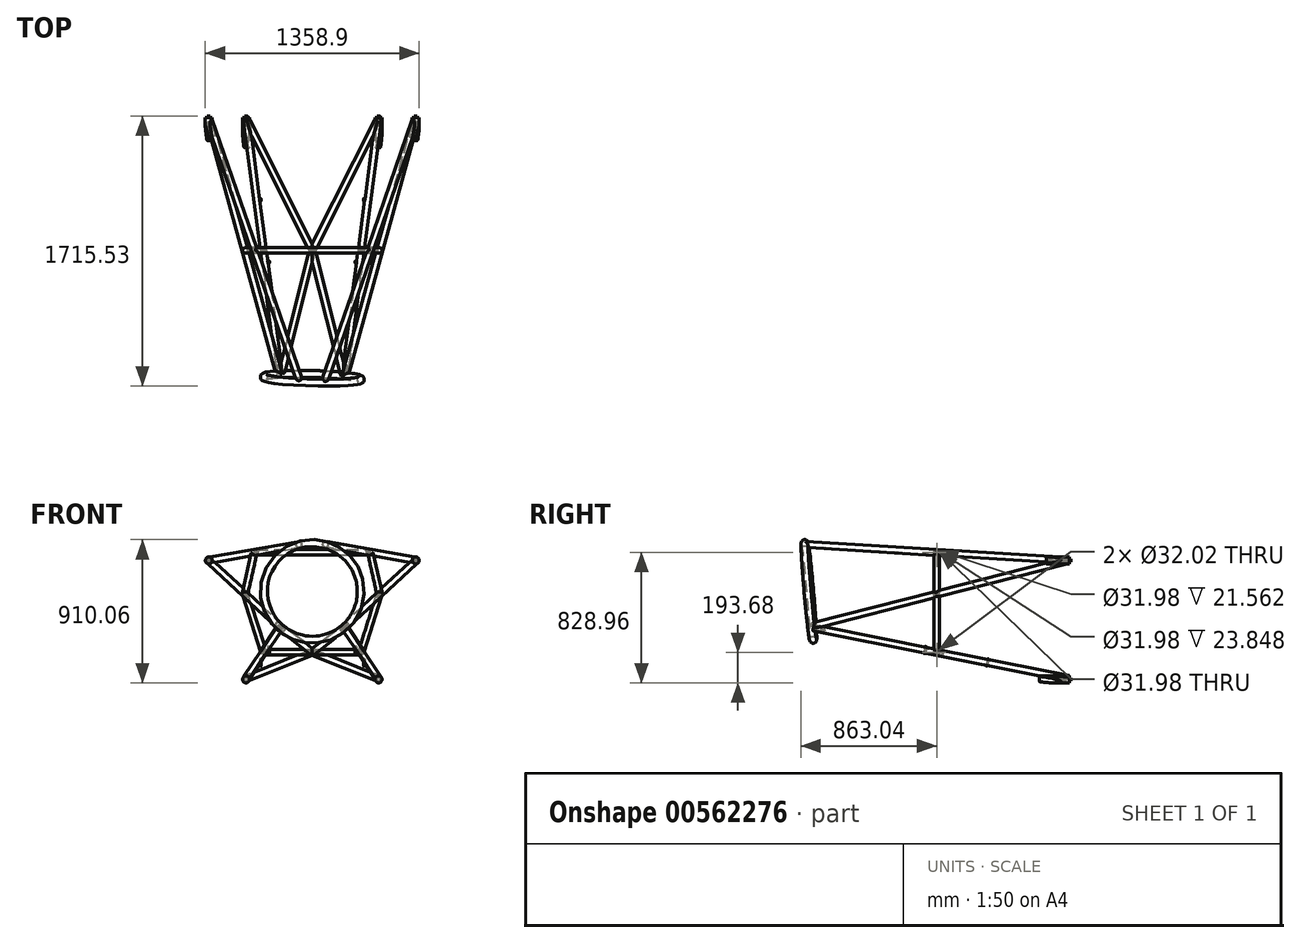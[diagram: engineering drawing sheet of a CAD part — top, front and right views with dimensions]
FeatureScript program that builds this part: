
annotation { "Feature Type Name" : "Feature", "Feature Type Description" : "" }
export const myFeature = defineFeature(function(context is Context, id is Id, definition is map)
    precondition{}
    {
        {
            var Q0;
            Q0=qCreatedBy(makeId("Front.planeOp"),FACE);
            var sketch = newSketch(context, id + "F0", { "sketchPlane" : qUnion([Q0])});
            skCircle(sketch, "E0", {"center": v(0, 0) * mm, "radius": 285.75 * mm});
            skPoint(sketch, "E1", {"position": v(0, 285.75) * mm});
            skPoint(sketch, "E2", {"position": v(0, -285.75) * mm});
            skPoint(sketch, "E3", {"position": v(285.75, 0) * mm});
            skPoint(sketch, "E4", {"position": v(-285.75, 0) * mm});
            skLineSegment(sketch, "E5", {"start": v(0, 285.75) * mm, "end": v(0, -285.75) * mm, "construction": true});
            skLineSegment(sketch, "E6", {"start": v(285.75, 0) * mm, "end": v(-285.75, 0) * mm, "construction": true});
            skSolve(sketch);
        }
        {
            var Q0;
            Q0=qCreatedBy(makeId("Right.planeOp"),FACE);
            var sketch = newSketch(context, id + "F1", { "sketchPlane" : qUnion([Q0])});
            skCircle(sketch, "E7", {"center": v(0, 307.98) * mm, "radius": 22.23 * mm});
            skSolve(sketch);
        }
        {
            var Q0;
            Q0=qSketchRegion(id+"F1",true);
            var Q1;
            Q1=sQuery(id+"F0.wireOp",EDGE,"E0");
            revolve(context, id + "F2", {"surfaceOperationType" : NewSurfaceOperationType.NEW, "entities" : qUnion([Q0]), "axis" : qUnion([Q1]), "revolveType" : RevolveType.FULL});
        }
        {
            var Q0;
            Q0=qCreatedBy(makeId("Front.planeOp"),FACE);
            var sketch = newSketch(context, id + "F3", { "sketchPlane" : qUnion([Q0])});
            skCircle(sketch, "E8", {"center": v(0, 0) * mm, "radius": 307.98 * mm, "construction": true});
            skSolve(sketch);
        }
        {
            var Q0;
            Q0=qCreatedBy(makeId("Front.planeOp"),FACE);
            cPlane(context, id + "F4", {"entities" : qUnion([Q0]), "cplaneType" : CPlaneType.OFFSET, "offset" : 1654.17 * mm, "oppositeDirection" : true, "width" : 152.4 * mm, "height" : 152.4 * mm});
        }
        {
            var Q0;
            Q0=qCreatedBy(makeId("Right.planeOp"),FACE);
            var sketch = newSketch(context, id + "F5", { "sketchPlane" : qUnion([Q0])});
            skLineSegment(sketch, "E9", {"start": v(1501.77, 196.85) * mm, "end": v(1665.29, 196.85) * mm});
            skLineSegment(sketch, "E10", {"start": v(1665.29, 196.85) * mm, "end": v(1665.29, 196.85) * mm});
            skLineSegment(sketch, "E11", {"start": v(1665.29, 187.33) * mm, "end": v(1654.18, 187.33) * mm});
            skLineSegment(sketch, "E12", {"start": v(1654.18, 187.33) * mm, "end": v(1654.18, 174.63) * mm});
            skLineSegment(sketch, "E13", {"start": v(1654.18, 174.63) * mm, "end": v(1501.78, 174.63) * mm});
            skLineSegment(sketch, "E14", {"start": v(1501.78, 174.63) * mm, "end": v(1501.78, 178.4) * mm});
            skLineSegment(sketch, "E15", {"start": v(1501.77, 178.4) * mm, "end": v(1638.3, 178.4) * mm});
            skLineSegment(sketch, "E16", {"start": v(1641.48, 181.57) * mm, "end": v(1641.48, 191.3) * mm});
            skLineSegment(sketch, "E17", {"start": v(1641.48, 196.85) * mm, "end": v(1665.29, 196.85) * mm, "construction": true});
            skLineSegment(sketch, "E18", {"start": v(1665.29, 196.85) * mm, "end": v(1665.29, 191.3) * mm});
            skPoint(sketch, "E19.visualSharp", {"position": v(1641.48, 178.4) * mm});
            skArc(sketch, "E19.filletArc", {"start": v(1638.3, 178.4) * mm, "mid": v(1640.55, 179.32) * mm, "end": v(1641.48, 181.57) * mm});
            skLineSegment(sketch, "E20", {"start": v(1641.48, 191.3) * mm, "end": v(1665.29, 191.3) * mm});
            skLineSegment(sketch, "E21", {"start": v(1641.48, 191.3) * mm, "end": v(1641.48, 196.85) * mm, "construction": true});
            skLineSegment(sketch, "E22", {"start": v(1665.29, 191.3) * mm, "end": v(1665.29, 187.33) * mm});
            skLineSegment(sketch, "E23", {"start": v(1501.77, 196.85) * mm, "end": v(1501.77, 178.4) * mm});
            skSolve(sketch);
        }
        {
            var Q0;
            Q0=qSketchRegion(id+"F5",true);
            var Q1;
            Q1=sQuery(id+"F5.wireOp",EDGE,"E9");
            revolve(context, id + "F6", {"surfaceOperationType" : NewSurfaceOperationType.NEW, "entities" : qUnion([Q0]), "axis" : qUnion([Q1]), "revolveType" : RevolveType.FULL});
        }
        {
            var Q0;
            Q0=qCreatedBy(makeId("Right.planeOp"),FACE);
            var sketch = newSketch(context, id + "F7", { "sketchPlane" : qUnion([Q0])});
            skLineSegment(sketch, "E24", {"start": v(1501.78, 219.08) * mm, "end": v(1603.38, 219.08) * mm});
            skLineSegment(sketch, "E25", {"start": v(1603.38, 219.08) * mm, "end": v(1513.37, 203.2) * mm});
            skLineSegment(sketch, "E26", {"start": v(1508.13, 196.95) * mm, "end": v(1508.13, 174.63) * mm});
            skLineSegment(sketch, "E27", {"start": v(1508.13, 174.63) * mm, "end": v(1501.78, 174.63) * mm});
            skLineSegment(sketch, "E28", {"start": v(1501.78, 174.63) * mm, "end": v(1501.78, 219.08) * mm});
            skPoint(sketch, "E29.visualSharp", {"position": v(1508.13, 202.28) * mm});
            skArc(sketch, "E29.filletArc", {"start": v(1513.37, 203.2) * mm, "mid": v(1509.61, 201.03) * mm, "end": v(1508.13, 196.95) * mm});
            skLineSegment(sketch, "E30", {"start": v(1501.78, 196.85) * mm, "end": v(1665.29, 196.85) * mm, "construction": true});
            skSolve(sketch);
        }
        {
            var Q0;
            Q0=qSketchRegion(id+"F7",true);
            extrude(context, id + "F8", {"entities" : qUnion([Q0]), "operationType" : NewBodyOperationType.REMOVE, "endBound" : BoundingType.THROUGH_ALL, "depth" : 25.4 * mm, "offsetDistance" : 25.4 * mm, "hasSecondDirection" : true, "secondDirectionBound" : BoundingType.THROUGH_ALL, "secondDirectionOppositeDirection" : true, "secondDirectionDepth" : 25.4 * mm});
        }
        {
            var Q0;
            Q0=makeQuery(id+"F6.opRevolve","SWEPT_BODY",BODY,{"disambiguationData":[OSD([sQuery(id+"F5.wireOp",EDGE,"E11"),sQuery(id+"F5.wireOp",EDGE,"E12"),sQuery(id+"F5.wireOp",EDGE,"E13"),sQuery(id+"F5.wireOp",EDGE,"E14"),sQuery(id+"F5.wireOp",EDGE,"E15"),sQuery(id+"F5.wireOp",EDGE,"E16"),sQuery(id+"F5.wireOp",EDGE,"E19.filletArc"),sQuery(id+"F5.wireOp",EDGE,"E20"),sQuery(id+"F5.wireOp",EDGE,"E22")])]});
            var Q1;
            Q1=qCreatedBy(makeId("Right.planeOp"),FACE);
            transform(context, id + "F9", {"entities" : qUnion([Q0]), "transformType" : TransformType.TRANSLATION_DISTANCE, "transformDirection" : qUnion([Q1]), "distance" : 657.22 * mm, "makeCopy" : true});
        }
        {
            var Q0;
            Q0=makeQuery(id+"F6.opRevolve","SWEPT_BODY",BODY,{"disambiguationData":[OSD([sQuery(id+"F5.wireOp",EDGE,"E11"),sQuery(id+"F5.wireOp",EDGE,"E12"),sQuery(id+"F5.wireOp",EDGE,"E13"),sQuery(id+"F5.wireOp",EDGE,"E14"),sQuery(id+"F5.wireOp",EDGE,"E15"),sQuery(id+"F5.wireOp",EDGE,"E16"),sQuery(id+"F5.wireOp",EDGE,"E19.filletArc"),sQuery(id+"F5.wireOp",EDGE,"E20"),sQuery(id+"F5.wireOp",EDGE,"E22")])]});
            var Q1;
            Q1=qCreatedBy(makeId("Right.planeOp"),FACE);
            transform(context, id + "F10", {"entities" : qUnion([Q0]), "transformType" : TransformType.TRANSLATION_DISTANCE, "transformDirection" : qUnion([Q1]), "distance" : 657.22 * mm, "oppositeDirection" : true, "makeCopy" : false});
        }
        {
            var Q0;
            Q0=qCreatedBy(makeId("Right.planeOp"),FACE);
            var sketch = newSketch(context, id + "F11", { "sketchPlane" : qUnion([Q0])});
            skLineSegment(sketch, "E31", {"start": v(1457.33, -558.8) * mm, "end": v(1665.29, -558.8) * mm});
            skLineSegment(sketch, "E32", {"start": v(1665.29, -558.8) * mm, "end": v(1665.29, -558.8) * mm});
            skLineSegment(sketch, "E33", {"start": v(1665.29, -568.32) * mm, "end": v(1654.18, -568.32) * mm});
            skLineSegment(sketch, "E34", {"start": v(1654.18, -568.32) * mm, "end": v(1654.18, -581.02) * mm});
            skLineSegment(sketch, "E35", {"start": v(1654.18, -581.02) * mm, "end": v(1457.33, -581.02) * mm});
            skLineSegment(sketch, "E36", {"start": v(1457.33, -581.02) * mm, "end": v(1457.33, -577.26) * mm});
            skLineSegment(sketch, "E37", {"start": v(1457.33, -577.26) * mm, "end": v(1638.3, -577.26) * mm});
            skLineSegment(sketch, "E38", {"start": v(1641.48, -574.08) * mm, "end": v(1641.48, -564.36) * mm});
            skLineSegment(sketch, "E39", {"start": v(1641.48, -558.8) * mm, "end": v(1665.29, -558.8) * mm, "construction": true});
            skLineSegment(sketch, "E40", {"start": v(1665.29, -558.8) * mm, "end": v(1665.29, -564.36) * mm});
            skPoint(sketch, "E41.visualSharp", {"position": v(1641.48, -577.26) * mm});
            skArc(sketch, "E41.filletArc", {"start": v(1638.3, -577.26) * mm, "mid": v(1640.55, -576.33) * mm, "end": v(1641.48, -574.08) * mm});
            skLineSegment(sketch, "E42", {"start": v(1641.48, -564.36) * mm, "end": v(1665.29, -564.36) * mm});
            skLineSegment(sketch, "E43", {"start": v(1641.48, -564.36) * mm, "end": v(1641.48, -558.8) * mm, "construction": true});
            skLineSegment(sketch, "E44", {"start": v(1665.29, -564.36) * mm, "end": v(1665.29, -564.36) * mm});
            skLineSegment(sketch, "E45", {"start": v(1665.29, -564.36) * mm, "end": v(1665.29, -568.32) * mm});
            skLineSegment(sketch, "E46", {"start": v(1457.33, -577.26) * mm, "end": v(1457.33, -558.8) * mm});
            skSolve(sketch);
        }
        {
            var Q0;
            Q0=qSketchRegion(id+"F11",true);
            var Q1;
            Q1=sQuery(id+"F11.wireOp",EDGE,"E31");
            revolve(context, id + "F12", {"surfaceOperationType" : NewSurfaceOperationType.NEW, "entities" : qUnion([Q0]), "axis" : qUnion([Q1]), "revolveType" : RevolveType.FULL});
        }
        {
            var Q0;
            Q0=qCreatedBy(makeId("Right.planeOp"),FACE);
            var sketch = newSketch(context, id + "F13", { "sketchPlane" : qUnion([Q0])});
            skLineSegment(sketch, "E47", {"start": v(1457.33, -536.57) * mm, "end": v(1603.38, -536.57) * mm});
            skLineSegment(sketch, "E48", {"start": v(1603.38, -536.57) * mm, "end": v(1468.92, -560.28) * mm});
            skLineSegment(sketch, "E49", {"start": v(1463.68, -566.54) * mm, "end": v(1463.68, -581.02) * mm});
            skLineSegment(sketch, "E50", {"start": v(1463.68, -581.02) * mm, "end": v(1457.33, -581.02) * mm});
            skLineSegment(sketch, "E51", {"start": v(1457.33, -581.02) * mm, "end": v(1457.33, -536.57) * mm});
            skPoint(sketch, "E52.visualSharp", {"position": v(1463.68, -561.2) * mm});
            skArc(sketch, "E52.filletArc", {"start": v(1468.92, -560.28) * mm, "mid": v(1465.16, -562.45) * mm, "end": v(1463.68, -566.54) * mm});
            skLineSegment(sketch, "E53", {"start": v(1457.33, -558.8) * mm, "end": v(1665.29, -558.8) * mm, "construction": true});
            skSolve(sketch);
        }
        {
            var Q0;
            Q0=qSketchRegion(id+"F13",true);
            extrude(context, id + "F14", {"entities" : qUnion([Q0]), "operationType" : NewBodyOperationType.REMOVE, "endBound" : BoundingType.THROUGH_ALL, "depth" : 25.4 * mm, "offsetDistance" : 25.4 * mm, "hasSecondDirection" : true, "secondDirectionBound" : BoundingType.THROUGH_ALL, "secondDirectionOppositeDirection" : true, "secondDirectionDepth" : 25.4 * mm});
        }
        {
            var Q0;
            Q0=makeQuery(id+"F12.opRevolve","SWEPT_BODY",BODY,{"disambiguationData":[OSD([sQuery(id+"F11.wireOp",EDGE,"E33"),sQuery(id+"F11.wireOp",EDGE,"E34"),sQuery(id+"F11.wireOp",EDGE,"E35"),sQuery(id+"F11.wireOp",EDGE,"E36"),sQuery(id+"F11.wireOp",EDGE,"E37"),sQuery(id+"F11.wireOp",EDGE,"E38"),sQuery(id+"F11.wireOp",EDGE,"E41.filletArc"),sQuery(id+"F11.wireOp",EDGE,"E42"),sQuery(id+"F11.wireOp",EDGE,"E45")])]});
            var Q1;
            Q1=qCreatedBy(makeId("Right.planeOp"),FACE);
            transform(context, id + "F15", {"entities" : qUnion([Q0]), "transformType" : TransformType.TRANSLATION_DISTANCE, "transformDirection" : qUnion([Q1]), "distance" : 420.7 * mm, "makeCopy" : true});
        }
        {
            var Q0;
            Q0=makeQuery(id+"F12.opRevolve","SWEPT_BODY",BODY,{"disambiguationData":[OSD([sQuery(id+"F11.wireOp",EDGE,"E33"),sQuery(id+"F11.wireOp",EDGE,"E34"),sQuery(id+"F11.wireOp",EDGE,"E35"),sQuery(id+"F11.wireOp",EDGE,"E36"),sQuery(id+"F11.wireOp",EDGE,"E37"),sQuery(id+"F11.wireOp",EDGE,"E38"),sQuery(id+"F11.wireOp",EDGE,"E41.filletArc"),sQuery(id+"F11.wireOp",EDGE,"E42"),sQuery(id+"F11.wireOp",EDGE,"E45")])]});
            var Q1;
            Q1=qCreatedBy(makeId("Right.planeOp"),FACE);
            transform(context, id + "F16", {"entities" : qUnion([Q0]), "transformType" : TransformType.TRANSLATION_DISTANCE, "transformDirection" : qUnion([Q1]), "distance" : 420.7 * mm, "oppositeDirection" : true, "makeCopy" : false});
        }
        {
            var Q0;
            Q0=makeQuery(id+"F2.opRevolve","SWEPT_BODY",BODY,{"disambiguationData":[OSD([sQuery(id+"F1.wireOp",EDGE,"E7")])]});
            var Q1;
            Q1=sQuery(id+"F0.wireOp",EDGE,"E5");
            transform(context, id + "F17", {"entities" : qUnion([Q0]), "transformType" : TransformType.ROTATION, "transformAxis" : qUnion([Q1]), "angle" : 1.5 * degree, "makeCopy" : false});
        }
        {
            var Q0;
            Q0=makeQuery(id+"F2.opRevolve","SWEPT_BODY",BODY,{"disambiguationData":[OSD([sQuery(id+"F1.wireOp",EDGE,"E7")])]});
            var Q1;
            Q1=sQuery(id+"F0.wireOp",EDGE,"E6");
            transform(context, id + "F18", {"entities" : qUnion([Q0]), "transformType" : TransformType.ROTATION, "transformAxis" : qUnion([Q1]), "angle" : 5 * degree, "oppositeDirection" : true, "makeCopy" : false});
        }
        {
            var Q0;
            Q0=makeQuery(id+"F9.opPattern","COPY",BODY,{"derivedFrom":makeQuery(id+"F6.opRevolve","SWEPT_BODY",BODY,{"disambiguationData":[OSD([sQuery(id+"F5.wireOp",EDGE,"E11"),sQuery(id+"F5.wireOp",EDGE,"E12"),sQuery(id+"F5.wireOp",EDGE,"E13"),sQuery(id+"F5.wireOp",EDGE,"E14"),sQuery(id+"F5.wireOp",EDGE,"E15"),sQuery(id+"F5.wireOp",EDGE,"E16"),sQuery(id+"F5.wireOp",EDGE,"E19.filletArc"),sQuery(id+"F5.wireOp",EDGE,"E20"),sQuery(id+"F5.wireOp",EDGE,"E22")])]}),"instanceName":"1"});
            var Q1;
            Q1=makeQuery(id+"F9.opPattern","COPY",EDGE,{"derivedFrom":makeQuery(id+"F6.opRevolve","SWEPT_EDGE",EDGE,{"disambiguationData":[OSD([sQuery(id+"F5.wireOp",EDGE,"E20"),sQuery(id+"F5.wireOp",EDGE,"E22")])]}),"instanceName":"1"});
            transform(context, id + "F19", {"entities" : qUnion([Q0]), "transformType" : TransformType.ROTATION, "transformAxis" : qUnion([Q1]), "angle" : 73 * degree, "oppositeDirection" : true, "makeCopy" : false});
        }
        {
            var Q0;
            Q0=makeQuery(id+"F6.opRevolve","SWEPT_BODY",BODY,{"disambiguationData":[OSD([sQuery(id+"F5.wireOp",EDGE,"E11"),sQuery(id+"F5.wireOp",EDGE,"E12"),sQuery(id+"F5.wireOp",EDGE,"E13"),sQuery(id+"F5.wireOp",EDGE,"E14"),sQuery(id+"F5.wireOp",EDGE,"E15"),sQuery(id+"F5.wireOp",EDGE,"E16"),sQuery(id+"F5.wireOp",EDGE,"E19.filletArc"),sQuery(id+"F5.wireOp",EDGE,"E20"),sQuery(id+"F5.wireOp",EDGE,"E22")])]});
            var Q1;
            Q1=makeQuery(id+"F6.opRevolve","SWEPT_EDGE",EDGE,{"disambiguationData":[OSD([sQuery(id+"F5.wireOp",EDGE,"E20"),sQuery(id+"F5.wireOp",EDGE,"E22")])]});
            transform(context, id + "F20", {"entities" : qUnion([Q0]), "transformType" : TransformType.ROTATION, "transformAxis" : qUnion([Q1]), "angle" : 73 * degree, "makeCopy" : false});
        }
        {
            var Q0;
            Q0=makeQuery(id+"F15.opPattern","COPY",BODY,{"derivedFrom":makeQuery(id+"F12.opRevolve","SWEPT_BODY",BODY,{"disambiguationData":[OSD([sQuery(id+"F11.wireOp",EDGE,"E33"),sQuery(id+"F11.wireOp",EDGE,"E34"),sQuery(id+"F11.wireOp",EDGE,"E35"),sQuery(id+"F11.wireOp",EDGE,"E36"),sQuery(id+"F11.wireOp",EDGE,"E37"),sQuery(id+"F11.wireOp",EDGE,"E38"),sQuery(id+"F11.wireOp",EDGE,"E41.filletArc"),sQuery(id+"F11.wireOp",EDGE,"E42"),sQuery(id+"F11.wireOp",EDGE,"E45")])]}),"instanceName":"1"});
            var Q1;
            Q1=makeQuery(id+"F15.opPattern","COPY",EDGE,{"derivedFrom":makeQuery(id+"F12.opRevolve","SWEPT_EDGE",EDGE,{"disambiguationData":[OSD([sQuery(id+"F11.wireOp",EDGE,"E42"),sQuery(id+"F11.wireOp",EDGE,"E45")])]}),"instanceName":"1"});
            transform(context, id + "F21", {"entities" : qUnion([Q0]), "transformType" : TransformType.ROTATION, "transformAxis" : qUnion([Q1]), "angle" : 132 * degree, "oppositeDirection" : true, "makeCopy" : false});
        }
        {
            var Q0;
            Q0=makeQuery(id+"F12.opRevolve","SWEPT_BODY",BODY,{"disambiguationData":[OSD([sQuery(id+"F11.wireOp",EDGE,"E33"),sQuery(id+"F11.wireOp",EDGE,"E34"),sQuery(id+"F11.wireOp",EDGE,"E35"),sQuery(id+"F11.wireOp",EDGE,"E36"),sQuery(id+"F11.wireOp",EDGE,"E37"),sQuery(id+"F11.wireOp",EDGE,"E38"),sQuery(id+"F11.wireOp",EDGE,"E41.filletArc"),sQuery(id+"F11.wireOp",EDGE,"E42"),sQuery(id+"F11.wireOp",EDGE,"E45")])]});
            var Q1;
            Q1=makeQuery(id+"F12.opRevolve","SWEPT_EDGE",EDGE,{"disambiguationData":[OSD([sQuery(id+"F11.wireOp",EDGE,"E42"),sQuery(id+"F11.wireOp",EDGE,"E45")])]});
            transform(context, id + "F22", {"entities" : qUnion([Q0]), "transformType" : TransformType.ROTATION, "transformAxis" : qUnion([Q1]), "angle" : 132 * degree, "makeCopy" : false});
        }
        {
            var Q0;
            Q0=qCreatedBy(id+"F4.planeOp",FACE);
            cPlane(context, id + "F23", {"entities" : qUnion([Q0]), "cplaneType" : CPlaneType.OFFSET, "offset" : 841.38 * mm, "width" : 152.4 * mm, "height" : 152.4 * mm});
        }
        {
            var Q0;
            Q0=qCreatedBy(makeId("Right.planeOp"),FACE);
            var sketch = newSketch(context, id + "F24", { "sketchPlane" : qUnion([Q0])});
            skCircle(sketch, "E54", {"center": v(812.8, -387.35) * mm, "radius": 17.66 * mm});
            skLineSegment(sketch, "E55", {"start": v(812.8, -387.35) * mm, "end": v(660.4, -357.04) * mm, "construction": true});
            skLineSegment(sketch, "E56", {"start": v(812.8, -387.35) * mm, "end": v(660.4, -387.35) * mm, "construction": true});
            skLineSegment(sketch, "E57", {"start": v(812.8, -387.35) * mm, "end": v(842.53, -237.88) * mm, "construction": true});
            skCircle(sketch, "E58.0", {"center": v(812.8, -387.35) * mm, "radius": 16 * mm});
            skSolve(sketch);
        }
        {
            var Q0;
            Q0=sQuery(id+"F24.wireOp",EDGE,"E55");
            cPlane(context, id + "F25", {"entities" : qUnion([Q0]), "cplaneType" : CPlaneType.LINE_ANGLE, "offset" : 25.4 * mm, "angle" : 0 * degree, "width" : 152.4 * mm, "height" : 152.4 * mm});
        }
        {
            var Q0;
            Q0=qCreatedBy(id+"F25.planeOp",FACE);
            var sketch = newSketch(context, id + "F26", { "sketchPlane" : qUnion([Q0])});
            skLineSegment(sketch, "E59", {"start": v(-203.2, -44.03) * mm, "end": v(-420.69, -1724.26) * mm});
            skLineSegment(sketch, "E60", {"start": v(-203.2, -44.03) * mm, "end": v(0, -872.75) * mm});
            skLineSegment(sketch, "E61", {"start": v(0, -872.75) * mm, "end": v(-420.69, -1724.26) * mm});
            skLineSegment(sketch, "E62.MirrorCS", {"start": v(0, -872.75) * mm, "end": v(420.69, -1724.26) * mm});
            skLineSegment(sketch, "E63.MirrorCS", {"start": v(203.2, -44.03) * mm, "end": v(0, -872.75) * mm});
            skLineSegment(sketch, "E64.MirrorCS", {"start": v(203.2, -44.03) * mm, "end": v(420.69, -1724.26) * mm});
            skSolve(sketch);
        }
        {
            var Q0;
            Q0=sQuery(id+"F26.wireOp",EDGE,"E59");
            cPlane(context, id + "F27", {"entities" : qUnion([Q0]), "cplaneType" : CPlaneType.MID_PLANE, "offset" : 25.4 * mm, "width" : 152.4 * mm, "height" : 152.4 * mm});
        }
        {
            var Q0;
            Q0=qCreatedBy(id+"F27.planeOp",FACE);
            var sketch = newSketch(context, id + "F28", { "sketchPlane" : qUnion([Q0])});
            skCircle(sketch, "E65", {"center": v(195.87, -221.34) * mm, "radius": 19.05 * mm});
            skCircle(sketch, "E66.0", {"center": v(195.87, -221.34) * mm, "radius": 16.56 * mm});
            skSolve(sketch);
        }
        {
            var Q0;
            Q0=qSketchRegion(id+"F28",true);
            var Q1;
            Q1=makeQuery(id+"F12.opRevolve","SWEPT_FACE",FACE,{"disambiguationData":[OSD([sQuery(id+"F11.wireOp",EDGE,"E35")])]});
            var Q2;
            Q2=makeQuery(id+"F12.opRevolve","SWEPT_BODY",BODY,{"disambiguationData":[OSD([sQuery(id+"F11.wireOp",EDGE,"E31"),sQuery(id+"F11.wireOp",EDGE,"E33"),sQuery(id+"F11.wireOp",EDGE,"E34"),sQuery(id+"F11.wireOp",EDGE,"E35"),sQuery(id+"F11.wireOp",EDGE,"E36"),sQuery(id+"F11.wireOp",EDGE,"E40"),sQuery(id+"F11.wireOp",EDGE,"E45"),sQuery(id+"F11.wireOp",EDGE,"E46")])]});
            extrude(context, id + "F29", {"entities" : qUnion([Q0]), "operationType" : NewBodyOperationType.ADD, "depth" : 834.9 * mm, "endBoundEntityFace" : qUnion([Q1]), "endBoundEntityBody" : qUnion([Q2]), "offsetDistance" : 25.4 * mm, "hasSecondDirection" : true, "secondDirectionOppositeDirection" : true, "secondDirectionDepth" : 812.8 * mm});
        }
        {
            var Q0;
            Q0=sQuery(id+"F26.wireOp",EDGE,"E64.MirrorCS");
            cPlane(context, id + "F30", {"entities" : qUnion([Q0]), "cplaneType" : CPlaneType.MID_PLANE, "offset" : 25.4 * mm, "width" : 152.4 * mm, "height" : 152.4 * mm});
        }
        {
            var Q0;
            Q0=qCreatedBy(id+"F30.planeOp",FACE);
            var sketch = newSketch(context, id + "F31", { "sketchPlane" : qUnion([Q0])});
            skCircle(sketch, "E67", {"center": v(-195.87, -221.34) * mm, "radius": 19.05 * mm});
            skCircle(sketch, "E68.0", {"center": v(-195.87, -221.34) * mm, "radius": 16.64 * mm});
            skSolve(sketch);
        }
        {
            var Q0;
            Q0=qSketchRegion(id+"F31",true);
            var Q1;
            Q1=makeQuery(id+"F15.opPattern","COPY",FACE,{"derivedFrom":makeQuery(id+"F12.opRevolve","SWEPT_FACE",FACE,{"disambiguationData":[OSD([sQuery(id+"F11.wireOp",EDGE,"E35")])]}),"instanceName":"1"});
            extrude(context, id + "F32", {"entities" : qUnion([Q0]), "operationType" : NewBodyOperationType.ADD, "depth" : 847.34 * mm, "endBoundEntityFace" : qUnion([Q1]), "offsetDistance" : 25.4 * mm, "hasSecondDirection" : true, "secondDirectionOppositeDirection" : true, "secondDirectionDepth" : 816.6 * mm});
        }
        {
            var Q0;
            Q0=qSketchRegion(id+"F24",true);
            extrude(context, id + "F33", {"entities" : qUnion([Q0]), "operationType" : NewBodyOperationType.ADD, "oppositeDirection" : true, "depth" : 310.9 * mm, "offsetDistance" : 25.4 * mm, "hasSecondDirection" : true, "secondDirectionOppositeDirection" : false, "secondDirectionDepth" : 314.96 * mm});
        }
        {
            var Q0;
            Q0=sQuery(id+"F26.wireOp",EDGE,"E60");
            cPlane(context, id + "F34", {"entities" : qUnion([Q0]), "cplaneType" : CPlaneType.MID_PLANE, "offset" : 25.4 * mm, "width" : 152.4 * mm, "height" : 152.4 * mm});
        }
        {
            var Q0;
            Q0=qCreatedBy(id+"F34.planeOp",FACE);
            var sketch = newSketch(context, id + "F35", { "sketchPlane" : qUnion([Q0])});
            skCircle(sketch, "E69", {"center": v(207.84, -221.34) * mm, "radius": 19.05 * mm});
            skCircle(sketch, "E70.0", {"center": v(207.84, -221.34) * mm, "radius": 16.56 * mm});
            skSolve(sketch);
        }
        {
            var Q0;
            Q0=makeQuery(id+"F35.imprint","IMPRINT",FACE,{"disambiguationData":[TD([[makeQuery(id+"F35.imprint","IMPRINT",EDGE,{"derivedFrom":sQuery(id+"F35.wireOp",EDGE,"E69")}),1.0]])]});
            var Q1;
            Q1=makeQuery(id+"F0bZUNIE9ARQCuC_9.opExtrude","CAP_FACE",FACE,{"disambiguationData":[OSD([sQuery(id+"FQs5VrxEJPu7HWf_9.wireOp",EDGE,"Z0tjX9Jh-rcT5-KGF2-Hdfp-c0TFuIOMkkUb.bottom"),sQuery(id+"FQs5VrxEJPu7HWf_9.wireOp",EDGE,"Z0tjX9Jh-rcT5-KGF2-Hdfp-c0TFuIOMkkUb.top"),sQuery(id+"FQs5VrxEJPu7HWf_9.wireOp",EDGE,"Z0tjX9Jh-rcT5-KGF2-Hdfp-c0TFuIOMkkUb.left"),sQuery(id+"FQs5VrxEJPu7HWf_9.wireOp",EDGE,"Z0tjX9Jh-rcT5-KGF2-Hdfp-c0TFuIOMkkUb.right")])],"isStart":true});
            var Q2;
            Q2=makeQuery(id+"F2.opRevolve","SWEPT_BODY",BODY,{"disambiguationData":[OSD([sQuery(id+"F1.wireOp",EDGE,"E7")])]});
            var Q3;
            Q3=makeQuery(id+"F29.opExtrude","SWEPT_FACE",FACE,{"disambiguationData":[OSD([sQuery(id+"F28.wireOp",EDGE,"E65")])]});
            extrude(context, id + "F36", {"entities" : qUnion([Q0]), "operationType" : NewBodyOperationType.ADD, "depth" : 421.4 * mm, "endBoundEntityFace" : qUnion([Q1]), "endBoundEntityBody" : qUnion([Q2]), "offsetDistance" : 25.4 * mm, "hasSecondDirection" : true, "secondDirectionOppositeDirection" : true, "secondDirectionDepth" : 393.7 * mm, "secondDirectionBoundEntityFace" : qUnion([Q3])});
        }
        {
            var Q0;
            Q0=sQuery(id+"F26.wireOp",EDGE,"E63.MirrorCS");
            cPlane(context, id + "F37", {"entities" : qUnion([Q0]), "cplaneType" : CPlaneType.MID_PLANE, "offset" : 25.4 * mm, "width" : 152.4 * mm, "height" : 152.4 * mm});
        }
        {
            var Q0;
            Q0=qCreatedBy(id+"F37.planeOp",FACE);
            var sketch = newSketch(context, id + "F38", { "sketchPlane" : qUnion([Q0])});
            skCircle(sketch, "E71", {"center": v(-207.84, -221.34) * mm, "radius": 19.05 * mm});
            skCircle(sketch, "E72.0", {"center": v(-207.84, -221.34) * mm, "radius": 16.64 * mm});
            skSolve(sketch);
        }
        {
            var Q0;
            Q0=qSketchRegion(id+"F38",true);
            var Q1;
            Q1=makeQuery(id+"FKdSqRBJJScF7KS_12.opBoolean","COPY",FACE,{"derivedFrom":makeQuery(id+"FiDCOXsQ5TtwjaG_11.opExtrude","CAP_FACE",FACE,{"disambiguationData":[OSD([sQuery(id+"FQBkfejf2aEUZUS_10.wireOp",EDGE,"gjKXcAou-53FG-Y1Qx-ESph-NRVmfpsZ0WBW.bottom"),sQuery(id+"FQBkfejf2aEUZUS_10.wireOp",EDGE,"gjKXcAou-53FG-Y1Qx-ESph-NRVmfpsZ0WBW.top"),sQuery(id+"FQBkfejf2aEUZUS_10.wireOp",EDGE,"gjKXcAou-53FG-Y1Qx-ESph-NRVmfpsZ0WBW.left"),sQuery(id+"FQBkfejf2aEUZUS_10.wireOp",EDGE,"gjKXcAou-53FG-Y1Qx-ESph-NRVmfpsZ0WBW.right")])],"isStart":true})});
            var Q2;
            Q2=makeQuery(id+"F32.opExtrude","SWEPT_FACE",FACE,{"disambiguationData":[OSD([sQuery(id+"F31.wireOp",EDGE,"E67")])]});
            extrude(context, id + "F39", {"entities" : qUnion([Q0]), "operationType" : NewBodyOperationType.ADD, "depth" : 423.16 * mm, "endBoundEntityFace" : qUnion([Q1]), "offsetDistance" : 25.4 * mm, "hasSecondDirection" : true, "secondDirectionOppositeDirection" : true, "secondDirectionDepth" : 411.48 * mm, "secondDirectionBoundEntityFace" : qUnion([Q2])});
        }
        {
            var Q0;
            Q0=qCreatedBy(makeId("Right.planeOp"),FACE);
            var sketch = newSketch(context, id + "F40", { "sketchPlane" : qUnion([Q0])});
            skLineSegment(sketch, "E73", {"start": v(0, -225.67) * mm, "end": v(1647.95, 196.85) * mm, "construction": true});
            skLineSegment(sketch, "E74", {"start": v(823.97, 247.25) * mm, "end": v(833.28, 399.36) * mm, "construction": true});
            skLineSegment(sketch, "E75", {"start": v(823.97, -14.41) * mm, "end": v(786.12, 133.21) * mm, "construction": true});
            skLineSegment(sketch, "E76", {"start": v(1647.95, 196.85) * mm, "end": v(0, 297.64) * mm, "construction": true});
            skLineSegment(sketch, "E77", {"start": v(1647.95, 196.85) * mm, "end": v(1495.55, 196.85) * mm, "construction": true});
            skSolve(sketch);
        }
        {
            var Q0;
            Q0=sQuery(id+"F40.wireOp",EDGE,"E76");
            cPlane(context, id + "F41", {"entities" : qUnion([Q0]), "cplaneType" : CPlaneType.LINE_ANGLE, "offset" : 25.4 * mm, "angle" : 0 * degree, "width" : 152.4 * mm, "height" : 152.4 * mm});
        }
        {
            var Q0;
            Q0=qCreatedBy(id+"F41.planeOp",FACE);
            var sketch = newSketch(context, id + "F42", { "sketchPlane" : qUnion([Q0])});
            skLineSegment(sketch, "E78", {"start": v(-85.73, 18.06) * mm, "end": v(-657.22, -1632.75) * mm});
            skLineSegment(sketch, "E79", {"start": v(-85.73, 18.06) * mm, "end": v(-73.26, 54.06) * mm});
            skLineSegment(sketch, "E80.MirrorCS", {"start": v(85.72, 18.06) * mm, "end": v(657.23, -1632.75) * mm});
            skSolve(sketch);
        }
        {
            var Q0;
            Q0=sQuery(id+"F42.wireOp",EDGE,"E78");
            cPlane(context, id + "F43", {"entities" : qUnion([Q0]), "cplaneType" : CPlaneType.MID_PLANE, "offset" : 25.4 * mm, "width" : 152.4 * mm, "height" : 152.4 * mm});
        }
        {
            var Q0;
            Q0=qCreatedBy(id+"F43.planeOp",FACE);
            var sketch = newSketch(context, id + "F44", { "sketchPlane" : qUnion([Q0])});
            skCircle(sketch, "E81", {"center": v(86.92, 297.09) * mm, "radius": 19.05 * mm});
            skCircle(sketch, "E82.0", {"center": v(86.92, 297.09) * mm, "radius": 16.64 * mm});
            skSolve(sketch);
        }
        {
            var Q0;
            Q0=sQuery(id+"F26.wireOp",EDGE,"E61");
            cPlane(context, id + "F45", {"entities" : qUnion([Q0]), "cplaneType" : CPlaneType.MID_PLANE, "offset" : 25.4 * mm, "width" : 152.4 * mm, "height" : 152.4 * mm});
        }
        {
            var Q0;
            Q0=qCreatedBy(id+"F45.planeOp",FACE);
            var sketch = newSketch(context, id + "F46", { "sketchPlane" : qUnion([Q0])});
            skCircle(sketch, "E83", {"center": v(-386.58, -221.34) * mm, "radius": 19.05 * mm});
            skCircle(sketch, "E84.0", {"center": v(-386.58, -221.34) * mm, "radius": 16.56 * mm});
            skSolve(sketch);
        }
        {
            var Q0;
            Q0=qSketchRegion(id+"F46",true);
            var Q1;
            Q1=makeQuery(id+"F29.opExtrude","SWEPT_FACE",FACE,{"disambiguationData":[OSD([sQuery(id+"F28.wireOp",EDGE,"E65")])]});
            var Q2;
            Q2=makeQuery(id+"F0bZUNIE9ARQCuC_9.opExtrude","CAP_FACE",FACE,{"disambiguationData":[OSD([sQuery(id+"FQs5VrxEJPu7HWf_9.wireOp",EDGE,"Z0tjX9Jh-rcT5-KGF2-Hdfp-c0TFuIOMkkUb.bottom"),sQuery(id+"FQs5VrxEJPu7HWf_9.wireOp",EDGE,"Z0tjX9Jh-rcT5-KGF2-Hdfp-c0TFuIOMkkUb.top"),sQuery(id+"FQs5VrxEJPu7HWf_9.wireOp",EDGE,"Z0tjX9Jh-rcT5-KGF2-Hdfp-c0TFuIOMkkUb.left"),sQuery(id+"FQs5VrxEJPu7HWf_9.wireOp",EDGE,"Z0tjX9Jh-rcT5-KGF2-Hdfp-c0TFuIOMkkUb.right")])],"isStart":true});
            var Q3;
            Q3=makeQuery(id+"F33.opExtrude","SWEPT_BODY",BODY,{"disambiguationData":[OSD([sQuery(id+"F24.wireOp",EDGE,"E54"),sQuery(id+"F24.wireOp",EDGE,"E58.0")])]});
            extrude(context, id + "F47", {"entities" : qUnion([Q0]), "depth" : 455.42 * mm, "endBoundEntityFace" : qUnion([Q1]), "offsetDistance" : 25.4 * mm, "hasSecondDirection" : true, "secondDirectionOppositeDirection" : true, "secondDirectionDepth" : 471.17 * mm, "secondDirectionBoundEntityFace" : qUnion([Q2]), "secondDirectionBoundEntityBody" : qUnion([Q3])});
        }
        {
            var Q0;
            Q0=qSketchRegion(id+"F44",true);
            extrude(context, id + "F48", {"entities" : qUnion([Q0]), "operationType" : NewBodyOperationType.ADD, "depth" : 866.14 * mm, "offsetDistance" : 25.4 * mm, "hasSecondDirection" : true, "secondDirectionOppositeDirection" : true, "secondDirectionDepth" : 900.68 * mm});
        }
        {
            var Q0;
            Q0=sQuery(id+"F42.wireOp",EDGE,"E80.MirrorCS");
            cPlane(context, id + "F49", {"entities" : qUnion([Q0]), "cplaneType" : CPlaneType.MID_PLANE, "offset" : 25.4 * mm, "width" : 152.4 * mm, "height" : 152.4 * mm});
        }
        {
            var Q0;
            Q0=qCreatedBy(id+"F49.planeOp",FACE);
            var sketch = newSketch(context, id + "F50", { "sketchPlane" : qUnion([Q0])});
            skCircle(sketch, "E85", {"center": v(-86.92, 297.09) * mm, "radius": 19.05 * mm});
            skCircle(sketch, "E86.0", {"center": v(-86.92, 297.09) * mm, "radius": 16.64 * mm});
            skSolve(sketch);
        }
        {
            var Q0;
            Q0=qSketchRegion(id+"F50",true);
            extrude(context, id + "F51", {"entities" : qUnion([Q0]), "operationType" : NewBodyOperationType.ADD, "depth" : 868.93 * mm, "offsetDistance" : 25.4 * mm, "hasSecondDirection" : true, "secondDirectionOppositeDirection" : true, "secondDirectionDepth" : 901.45 * mm});
        }
        {
            var Q0;
            Q0=qCreatedBy(makeId("Right.planeOp"),FACE);
            var sketch = newSketch(context, id + "F52", { "sketchPlane" : qUnion([Q0])});
            skCircle(sketch, "E87", {"center": v(812.8, 247.93) * mm, "radius": 17.46 * mm});
            skCircle(sketch, "E88.0", {"center": v(812.8, 247.93) * mm, "radius": 15.99 * mm});
            skSolve(sketch);
        }
        {
            var Q0;
            Q0=qSketchRegion(id+"F52",true);
            var Q1;
            Q1=makeQuery(id+"F51.opExtrude","SWEPT_FACE",FACE,{"disambiguationData":[OSD([sQuery(id+"F50.wireOp",EDGE,"E85")])]});
            extrude(context, id + "F53", {"entities" : qUnion([Q0]), "operationType" : NewBodyOperationType.ADD, "oppositeDirection" : true, "depth" : 366 * mm, "offsetDistance" : 25.4 * mm, "hasSecondDirection" : true, "secondDirectionOppositeDirection" : false, "secondDirectionDepth" : 368.3 * mm, "secondDirectionBoundEntityFace" : qUnion([Q1])});
        }
        {
            var Q0;
            Q0=sQuery(id+"F40.wireOp",EDGE,"E73");
            cPlane(context, id + "F54", {"entities" : qUnion([Q0]), "cplaneType" : CPlaneType.LINE_ANGLE, "offset" : 25.4 * mm, "angle" : 0 * degree, "width" : 152.4 * mm, "height" : 152.4 * mm});
        }
        {
            var Q0;
            Q0=qCreatedBy(id+"F54.planeOp",FACE);
            var sketch = newSketch(context, id + "F55", { "sketchPlane" : qUnion([Q0])});
            skLineSegment(sketch, "E89", {"start": v(-203.2, -56.05) * mm, "end": v(-657.23, 1645.1) * mm});
            skLineSegment(sketch, "E90.MirrorCS", {"start": v(203.2, -56.05) * mm, "end": v(657.23, 1645.1) * mm});
            skSolve(sketch);
        }
        {
            var Q0;
            Q0=sQuery(id+"F55.wireOp",EDGE,"E89");
            cPlane(context, id + "F56", {"entities" : qUnion([Q0]), "cplaneType" : CPlaneType.MID_PLANE, "offset" : 25.4 * mm, "width" : 152.4 * mm, "height" : 152.4 * mm});
        }
        {
            var Q0;
            Q0=qCreatedBy(id+"F56.planeOp",FACE);
            var sketch = newSketch(context, id + "F57", { "sketchPlane" : qUnion([Q0])});
            skCircle(sketch, "E91", {"center": v(210.78, -218.6) * mm, "radius": 19.05 * mm});
            skCircle(sketch, "E92.0", {"center": v(210.78, -218.6) * mm, "radius": 16.64 * mm});
            skSolve(sketch);
        }
        {
            var Q0;
            Q0=makeQuery(id+"F57.imprint","IMPRINT",FACE,{"disambiguationData":[TD([[makeQuery(id+"F57.imprint","IMPRINT",EDGE,{"derivedFrom":sQuery(id+"F57.wireOp",EDGE,"E91")}),1.0]])]});
            var Q1;
            Q1=makeQuery(id+"F48.opExtrude","SWEPT_FACE",FACE,{"disambiguationData":[OSD([sQuery(id+"F44.wireOp",EDGE,"E81")])]});
            var Q2;
            Q2=makeQuery(id+"F6.opRevolve","SWEPT_BODY",BODY,{"disambiguationData":[OSD([sQuery(id+"F5.wireOp",EDGE,"E9"),sQuery(id+"F5.wireOp",EDGE,"E11"),sQuery(id+"F5.wireOp",EDGE,"E12"),sQuery(id+"F5.wireOp",EDGE,"E13"),sQuery(id+"F5.wireOp",EDGE,"E14"),sQuery(id+"F5.wireOp",EDGE,"E18"),sQuery(id+"F5.wireOp",EDGE,"E22"),sQuery(id+"F5.wireOp",EDGE,"E23")])]});
            var Q3;
            Q3=makeQuery(id+"F29.opExtrude","SWEPT_FACE",FACE,{"disambiguationData":[OSD([sQuery(id+"F28.wireOp",EDGE,"E65")])]});
            extrude(context, id + "F58", {"entities" : qUnion([Q0]), "operationType" : NewBodyOperationType.ADD, "depth" : 866.14 * mm, "endBoundEntityFace" : qUnion([Q1]), "endBoundEntityBody" : qUnion([Q2]), "offsetDistance" : 25.4 * mm, "hasSecondDirection" : true, "secondDirectionOppositeDirection" : true, "secondDirectionDepth" : 855.22 * mm, "secondDirectionBoundEntityFace" : qUnion([Q3])});
        }
        {
            var Q0;
            Q0=sQuery(id+"F55.wireOp",EDGE,"E90.MirrorCS");
            cPlane(context, id + "F59", {"entities" : qUnion([Q0]), "cplaneType" : CPlaneType.MID_PLANE, "offset" : 25.4 * mm, "width" : 152.4 * mm, "height" : 152.4 * mm});
        }
        {
            var Q0;
            Q0=qCreatedBy(id+"F59.planeOp",FACE);
            var sketch = newSketch(context, id + "F60", { "sketchPlane" : qUnion([Q0])});
            skCircle(sketch, "E93", {"center": v(-210.78, -218.6) * mm, "radius": 19.05 * mm});
            skCircle(sketch, "E94.0", {"center": v(-210.78, -218.6) * mm, "radius": 16.64 * mm});
            skSolve(sketch);
        }
        {
            var Q0;
            Q0=qSketchRegion(id+"F60",true);
            var Q1;
            Q1=makeQuery(id+"F32.opExtrude","SWEPT_FACE",FACE,{"disambiguationData":[OSD([sQuery(id+"F31.wireOp",EDGE,"E67")])]});
            extrude(context, id + "F61", {"entities" : qUnion([Q0]), "operationType" : NewBodyOperationType.ADD, "depth" : 874.78 * mm, "offsetDistance" : 25.4 * mm, "hasSecondDirection" : true, "secondDirectionOppositeDirection" : true, "secondDirectionDepth" : 864.87 * mm, "secondDirectionBoundEntityFace" : qUnion([Q1])});
        }
        {
            var Q0;
            Q0=qCreatedBy(id+"F23.planeOp",FACE);
            var sketch = newSketch(context, id + "F62", { "sketchPlane" : qUnion([Q0])});
            skLineSegment(sketch, "E95", {"start": v(-368.3, 247.25) * mm, "end": v(-427.04, -14.43) * mm});
            skLineSegment(sketch, "E96", {"start": v(-427.04, -14.43) * mm, "end": v(-308.77, -389.57) * mm});
            skSolve(sketch);
        }
        {
            var Q0;
            Q0=sQuery(id+"F62.wireOp",EDGE,"E95");
            cPlane(context, id + "F63", {"entities" : qUnion([Q0]), "cplaneType" : CPlaneType.MID_PLANE, "offset" : 25.4 * mm, "width" : 152.4 * mm, "height" : 152.4 * mm});
        }
        {
            var Q0;
            Q0=qCreatedBy(id+"F63.planeOp",FACE);
            var sketch = newSketch(context, id + "F64", { "sketchPlane" : qUnion([Q0])});
            skCircle(sketch, "E97", {"center": v(-413.5, -812.8) * mm, "radius": 17.46 * mm});
            skCircle(sketch, "E98.0", {"center": v(-413.5, -812.8) * mm, "radius": 15.99 * mm});
            skSolve(sketch);
        }
        {
            var Q0;
            Q0=qSketchRegion(id+"F64",true);
            var Q1;
            Q1=makeQuery(id+"F58.opExtrude","SWEPT_FACE",FACE,{"disambiguationData":[OSD([sQuery(id+"F57.wireOp",EDGE,"E91")])]});
            var Q2;
            Q2=makeQuery(id+"F58.opExtrude","SWEPT_BODY",BODY,{"disambiguationData":[OSD([sQuery(id+"F57.wireOp",EDGE,"E91"),sQuery(id+"F57.wireOp",EDGE,"E92.0")])]});
            var Q3;
            Q3=makeQuery(id+"F53.opExtrude","SWEPT_FACE",FACE,{"disambiguationData":[OSD([sQuery(id+"F52.wireOp",EDGE,"E87")])]});
            var Q4;
            Q4=makeQuery(id+"F53.opExtrude","SWEPT_BODY",BODY,{"disambiguationData":[OSD([sQuery(id+"F52.wireOp",EDGE,"E87"),sQuery(id+"F52.wireOp",EDGE,"E88.0")])]});
            extrude(context, id + "F65", {"entities" : qUnion([Q0]), "depth" : 139.7 * mm, "endBoundEntityFace" : qUnion([Q1]), "endBoundEntityBody" : qUnion([Q2]), "offsetDistance" : 25.4 * mm, "hasSecondDirection" : true, "secondDirectionOppositeDirection" : true, "secondDirectionDepth" : 127 * mm, "secondDirectionBoundEntityFace" : qUnion([Q3]), "secondDirectionBoundEntityBody" : qUnion([Q4])});
        }
        {
            var Q0;
            Q0=sQuery(id+"F62.wireOp",EDGE,"E96");
            cPlane(context, id + "F66", {"entities" : qUnion([Q0]), "cplaneType" : CPlaneType.MID_PLANE, "offset" : 25.4 * mm, "width" : 152.4 * mm, "height" : 152.4 * mm});
        }
        {
            var Q0;
            Q0=qCreatedBy(id+"F66.planeOp",FACE);
            var sketch = newSketch(context, id + "F67", { "sketchPlane" : qUnion([Q0])});
            skCircle(sketch, "E99", {"center": v(-411.61, -812.8) * mm, "radius": 17.46 * mm});
            skCircle(sketch, "E100.0", {"center": v(-411.61, -812.8) * mm, "radius": 15.99 * mm});
            skSolve(sketch);
        }
        {
            var Q0;
            Q0=qSketchRegion(id+"F67",true);
            var Q1;
            Q1=makeQuery(id+"F29.opExtrude","SWEPT_BODY",BODY,{"disambiguationData":[OSD([sQuery(id+"F28.wireOp",EDGE,"E65"),sQuery(id+"F28.wireOp",EDGE,"E66.0")])]});
            var Q2;
            Q2=makeQuery(id+"F58.opExtrude","SWEPT_FACE",FACE,{"disambiguationData":[OSD([sQuery(id+"F57.wireOp",EDGE,"E91")])]});
            extrude(context, id + "F68", {"entities" : qUnion([Q0]), "depth" : 195.33 * mm, "endBoundEntityBody" : qUnion([Q1]), "offsetDistance" : 25.4 * mm, "hasSecondDirection" : true, "secondDirectionOppositeDirection" : true, "secondDirectionDepth" : 190.5 * mm, "secondDirectionBoundEntityFace" : qUnion([Q2])});
        }
        {
            var Q0;
            Q0=makeQuery(id+"F47.opExtrude","SWEPT_BODY",BODY,{"disambiguationData":[OSD([sQuery(id+"F46.wireOp",EDGE,"E83"),sQuery(id+"F46.wireOp",EDGE,"E84.0")])]});
            var Q1;
            Q1=makeQuery(id+"F65.opExtrude","SWEPT_BODY",BODY,{"disambiguationData":[OSD([sQuery(id+"F64.wireOp",EDGE,"E97"),sQuery(id+"F64.wireOp",EDGE,"E98.0")])]});
            var Q2;
            Q2=makeQuery(id+"F68.opExtrude","SWEPT_BODY",BODY,{"disambiguationData":[OSD([sQuery(id+"F67.wireOp",EDGE,"E99"),sQuery(id+"F67.wireOp",EDGE,"E100.0")])]});
            var Q3;
            Q3=qCreatedBy(makeId("Right.planeOp"),FACE);
            mirror(context, id + "F69", {"operationType" : NewBodyOperationType.ADD, "entities" : qUnion([Q0, Q1, Q2]), "mirrorPlane" : qUnion([Q3])});
        }
        {
            var Q0;
            Q0=qCreatedBy(id+"F25.planeOp",FACE);
            var sketch = newSketch(context, id + "F70", { "sketchPlane" : qUnion([Q0])});
            skCircle(sketch, "E101", {"center": v(277.7, -796.48) * mm, "radius": 4.76 * mm});
            skCircle(sketch, "E102.0", {"center": v(277.7, -796.48) * mm, "radius": 3.29 * mm});
            skCircle(sketch, "E103.0", {"center": v(328.89, -1199.8) * mm, "radius": 3.29 * mm});
            skCircle(sketch, "E104.0", {"center": v(328.89, -1199.8) * mm, "radius": 4.76 * mm});
            skSolve(sketch);
        }
        {
            var Q0;
            Q0 = qSketchRegion(id + "F70", true);
            extrude(context, id + "F71", {"entities" : qUnion([Q0]), "oppositeDirection" : true, "depth" : 22.35 * mm, "offsetDistance" : 25.4 * mm, "hasSecondDirection" : true, "secondDirectionOppositeDirection" : false, "secondDirectionDepth" : 22.1 * mm});
        }
        {
            var Q0;
            Q0=makeQuery(id+"F71.opExtrude","SWEPT_BODY",BODY,{"disambiguationData":[OSD([sQuery(id+"F70.wireOp",EDGE,"E101"),sQuery(id+"F70.wireOp",EDGE,"E102.0")])]});
            var Q1;
            Q1=makeQuery(id+"F71.opExtrude","SWEPT_BODY",BODY,{"disambiguationData":[OSD([sQuery(id+"F70.wireOp",EDGE,"E103.0"),sQuery(id+"F70.wireOp",EDGE,"E104.0")])]});
            var Q2;
            Q2=qCreatedBy(makeId("Right.planeOp"),FACE);
            mirror(context, id + "F72", {"operationType" : NewBodyOperationType.ADD, "entities" : qUnion([Q0, Q1]), "mirrorPlane" : qUnion([Q2])});
        }
    });
